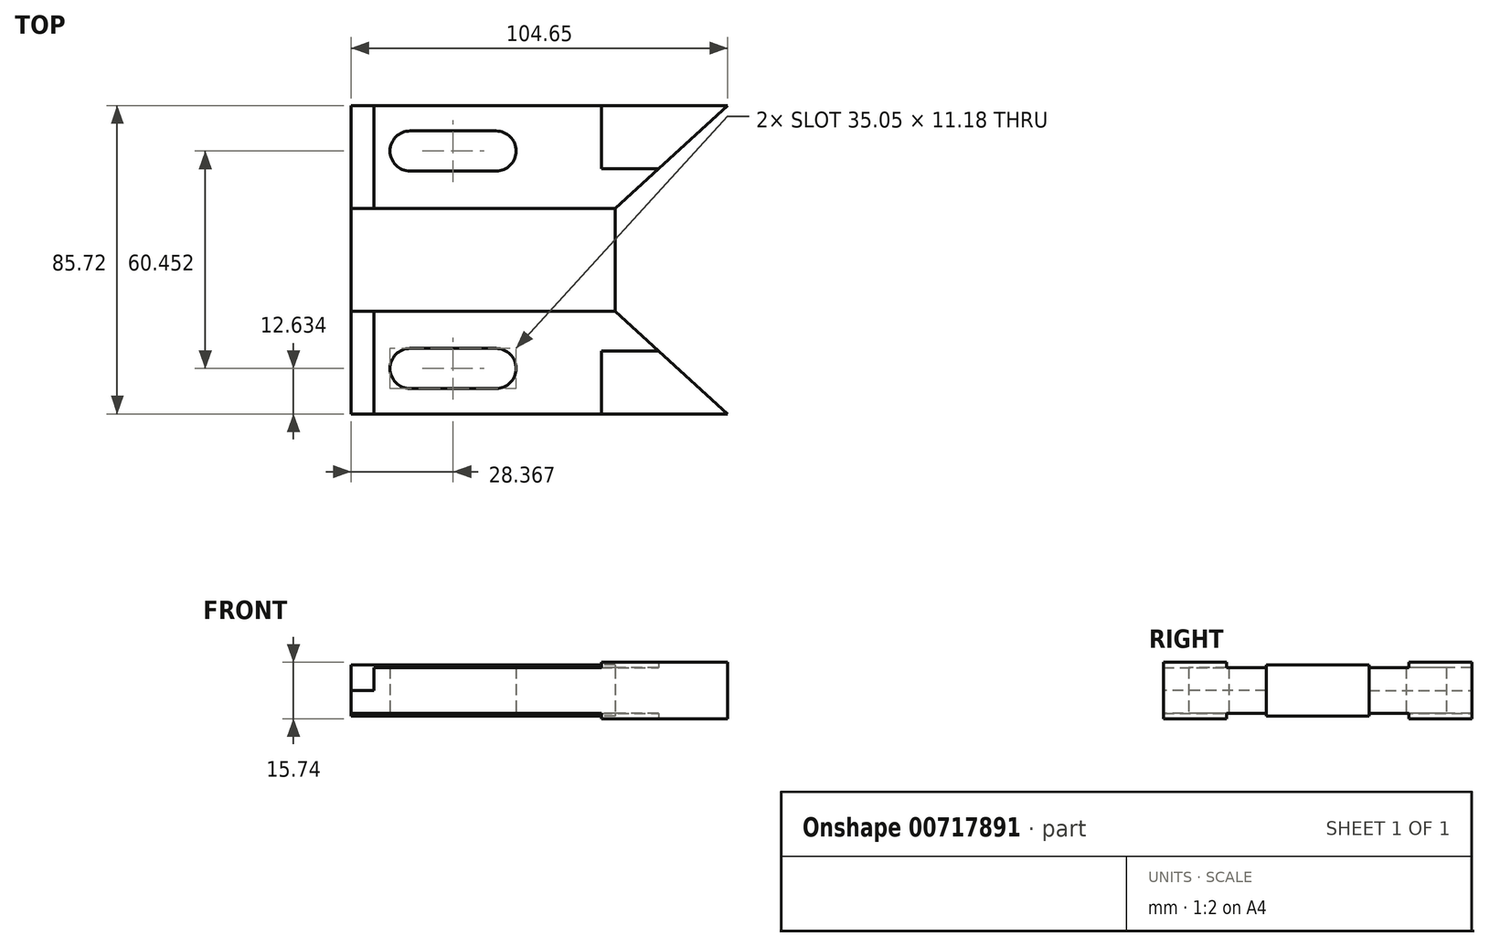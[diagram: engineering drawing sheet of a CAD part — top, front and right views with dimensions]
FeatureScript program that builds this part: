
annotation { "Feature Type Name" : "Feature", "Feature Type Description" : "" }
export const myFeature = defineFeature(function(context is Context, id is Id, definition is map)
    precondition{}
    {
        {
            var Q0;
            Q0=qCreatedBy(makeId("Top.planeOp"),FACE);
            var sketch = newSketch(context, id + "F0", { "sketchPlane" : qUnion([Q0])});
            skLineSegment(sketch, "E0.bottom", {"start": v(36.7, 14.29) * mm, "end": v(-36.7, 14.29) * mm});
            skLineSegment(sketch, "E0.top", {"start": v(36.7, -14.29) * mm, "end": v(-36.7, -14.29) * mm});
            skLineSegment(sketch, "E0.left", {"start": v(36.7, 14.29) * mm, "end": v(36.7, -14.29) * mm});
            skLineSegment(sketch, "E0.right", {"start": v(-36.7, 14.29) * mm, "end": v(-36.7, -14.29) * mm});
            skPoint(sketch, "E0.middle", {"position": v(0, 0) * mm});
            skSolve(sketch);
        }
        {
            var Q0;
            Q0=qCreatedBy(makeId("Top.planeOp"),FACE);
            var sketch = newSketch(context, id + "F1", { "sketchPlane" : qUnion([Q0])});
            skLineSegment(sketch, "E1", {"start": v(-36.7, 14.29) * mm, "end": v(-36.7, 42.86) * mm});
            skLineSegment(sketch, "E2", {"start": v(-36.7, 42.86) * mm, "end": v(67.95, 42.86) * mm});
            skLineSegment(sketch, "E3", {"start": v(67.95, 42.86) * mm, "end": v(36.7, 14.29) * mm});
            skLineSegment(sketch, "E4", {"start": v(36.7, 14.29) * mm, "end": v(-36.7, 14.29) * mm});
            skLineSegment(sketch, "E5", {"start": v(-30.35, 42.86) * mm, "end": v(-30.35, 14.29) * mm});
            skLineSegment(sketch, "E6", {"start": v(32.9, 42.86) * mm, "end": v(32.9, 25.34) * mm});
            skLineSegment(sketch, "E7", {"start": v(32.9, 25.34) * mm, "end": v(48.78, 25.34) * mm});
            skLineSegment(sketch, "E8.MirrorCS", {"start": v(-36.7, -14.29) * mm, "end": v(-36.7, -42.86) * mm});
            skLineSegment(sketch, "E9.MirrorCS", {"start": v(-30.35, -42.86) * mm, "end": v(-30.35, -14.29) * mm});
            skLineSegment(sketch, "E10.MirrorCS", {"start": v(-36.7, -42.86) * mm, "end": v(67.95, -42.86) * mm});
            skLineSegment(sketch, "E11.MirrorCS", {"start": v(36.7, -14.29) * mm, "end": v(-36.7, -14.29) * mm});
            skLineSegment(sketch, "E12.MirrorCS", {"start": v(67.95, -42.86) * mm, "end": v(36.7, -14.29) * mm});
            skLineSegment(sketch, "E13.MirrorCS", {"start": v(32.9, -42.86) * mm, "end": v(32.9, -25.34) * mm});
            skLineSegment(sketch, "E14.MirrorCS", {"start": v(32.9, -25.34) * mm, "end": v(48.78, -25.34) * mm});
            skLineSegment(sketch, "E15", {"start": v(-36.7, 14.29) * mm, "end": v(-36.7, 28.58) * mm, "construction": true});
            skArc(sketch, "E16", {"start": v(-20.27, 35.81) * mm, "mid": v(-25.86, 30.23) * mm, "end": v(-20.27, 24.64) * mm});
            skArc(sketch, "E17", {"start": v(3.6, 24.64) * mm, "mid": v(9.2, 30.23) * mm, "end": v(3.6, 35.81) * mm});
            skLineSegment(sketch, "E18", {"start": v(-20.27, 35.81) * mm, "end": v(3.6, 35.81) * mm});
            skLineSegment(sketch, "E19", {"start": v(-20.27, 24.64) * mm, "end": v(3.6, 24.64) * mm});
            skLineSegment(sketch, "E20.MirrorCS", {"start": v(-20.27, -24.64) * mm, "end": v(3.6, -24.64) * mm});
            skArc(sketch, "E21.MirrorCS", {"start": v(-20.27, -35.81) * mm, "mid": v(-25.86, -30.23) * mm, "end": v(-20.27, -24.64) * mm});
            skLineSegment(sketch, "E22.MirrorCS", {"start": v(-20.27, -35.81) * mm, "end": v(3.6, -35.81) * mm});
            skArc(sketch, "E23.MirrorCS", {"start": v(3.6, -24.64) * mm, "mid": v(9.2, -30.23) * mm, "end": v(3.6, -35.81) * mm});
            skPoint(sketch, "E24.trimOffspring.end.orphan", {"position": v(9.2, 30.23) * mm});
            skPoint(sketch, "E25.start.orphan", {"position": v(-25.86, 30.23) * mm});
            skSolve(sketch);
        }
        {
            var Q0;
            Q0 = qSketchRegion(id + "F0", true);
            extrude(context, id + "F2", {"entities" : qUnion([Q0]), "endBound" : BoundingType.SYMMETRIC, "depth" : 14.22 * mm, "offsetDistance" : 25.4 * mm});
        }
        {
            var Q0;
            {var subQ0=sQuery(id+"F1.wireOp",EDGE,"E5");Q0=makeQuery(id+"F1.imprint","IMPRINT",FACE,{"disambiguationData":[TD([[makeQuery(id+"F1.imprint","IMPRINT",EDGE,{"derivedFrom":subQ0}),1.0]])]});}
            var Q1;
            {var subQ3=sQuery(id+"F1.wireOp",EDGE,"E9.MirrorCS");Q1=makeQuery(id+"F1.imprint","IMPRINT",FACE,{"disambiguationData":[TD([[makeQuery(id+"F1.imprint","IMPRINT",EDGE,{"derivedFrom":subQ3}),-1.0]])]});}
            extrude(context, id + "F3", {"entities" : qUnion([Q0, Q1]), "operationType" : NewBodyOperationType.ADD, "endBound" : BoundingType.SYMMETRIC, "depth" : 12.7 * mm, "offsetDistance" : 25.4 * mm});
        }
        {
            var Q0;
            {var subQ0=sQuery(id+"F1.wireOp",EDGE,"E8.MirrorCS");Q0=makeQuery(id+"F1.imprint","IMPRINT",FACE,{"disambiguationData":[TD([[makeQuery(id+"F1.imprint","IMPRINT",EDGE,{"derivedFrom":subQ0}),1.0]])]});}
            var Q1;
            {var subQ0=sQuery(id+"F1.wireOp",EDGE,"E1");Q1=makeQuery(id+"F1.imprint","IMPRINT",FACE,{"disambiguationData":[TD([[makeQuery(id+"F1.imprint","IMPRINT",EDGE,{"derivedFrom":subQ0}),-1.0]])]});}
            extrude(context, id + "F4", {"entities" : qUnion([Q0, Q1]), "operationType" : NewBodyOperationType.ADD, "oppositeDirection" : true, "depth" : 6.38 * mm, "offsetDistance" : 25.4 * mm});
        }
        {
            var Q0;
            {var subQ0=sQuery(id+"F1.wireOp",EDGE,"E13.MirrorCS");Q0=makeQuery(id+"F1.imprint","IMPRINT",FACE,{"disambiguationData":[TD([[makeQuery(id+"F1.imprint","IMPRINT",EDGE,{"derivedFrom":subQ0}),-1.0]])]});}
            var Q1;
            {var subQ3=sQuery(id+"F1.wireOp",EDGE,"E6");Q1=makeQuery(id+"F1.imprint","IMPRINT",FACE,{"disambiguationData":[TD([[makeQuery(id+"F1.imprint","IMPRINT",EDGE,{"derivedFrom":subQ3}),1.0]])]});}
            extrude(context, id + "F5", {"entities" : qUnion([Q0, Q1]), "operationType" : NewBodyOperationType.ADD, "endBound" : BoundingType.SYMMETRIC, "depth" : 15.75 * mm, "offsetDistance" : 25.4 * mm});
        }
    });
